# Revit family: HS497-68_disk-nerez_volné vřeteno DN100-RFA_2019
name_source: partatom
category: Pipe Accessories
units: mm (PartAtom-declared; Revit-internal decimal feet)

## family parameters
Always vertical = Yes
Cut with Voids When Loaded = No
Part Type = Valve - Breaks Into
Round Connector Dimension = Use Diameter
Shared = No
Work Plane-Based = No

## types (43) — shared parameters
CAT0 = Yes
G1 = 90 mm
G2 = 23 mm
G22 = 11 mm
L2D = 216 mm
L2D_Min = 3048 mm
QmdConnectorList = 301;D;302;D
SW21 = No
URL = http://www.hydronic.cz
W2D = 1000 mm
magiPartTypeId = 305
magiProductFamilyId = 53cea81e6f374d17b8841d9c72ad77

## per-type parameters (varying)
- HS 497-68_DN100_PN16_volné vřeteno: A1=99 mm; A2=17 mm; B2=56 mm; B2__ve=-56 mm  [stored -0.183727 ft]; D=100 mm; DD=13 mm; DD1=16 mm; DR=147 mm; DR2=50 mm; Description=Mezipřírubová uzavírací klapka s volným vřetenem; nerezový disk, DN100; PN16; kvs512; E21=10 mm; E22=20 mm; E23=5 mm  [stored 0.0164042 ft]; E4=125 mm; E42=63 mm; E44=31 mm; F=11 mm; G=90 mm; H=30 mm; L=52 mm; L1=42 mm; L2=26 mm; L41=19 mm; L41__ve=-19 mm; L42=96 mm; L42__ve=-96 mm  [stored -0.314961 ft]; L4R=13 mm; L4R__ve=-13 mm; LH1=73 mm; LHH1=47 mm; LHH3=2 mm  [stored 0.00656168 ft]; LHL=220 mm; M4=44 mm; M41=66 mm; MC Product Code=124 100 (nerezový disk, s volným vřetenem; DN100; PN16, kvs512); MM20=25 mm; Manufacturer=Hydronic Systems Prague s.r.o.; NC=50 mm; R=50 mm; SW1=Yes; SW2=No; SW20=No; SW3=No; SW30=No; Type Comments=mezipřírubová; nerezový disk; PN16; -10~+110°C (krátkodobě +120°C); X1=25 mm; X11=61 mm; magiProductId=65d1b245f4f142c78569c0602d5754
- HS 497-68_DN100_PN16_převodové kolo: A1=99 mm; A2=17 mm; B2=56 mm; B2__ve=-56 mm  [stored -0.183727 ft]; D=100 mm; DD=13 mm; DD1=16 mm; DR=147 mm; DR2=50 mm; Description=Mezipřírubová uzavírací klapka s převodovým kolem; nerezový disk, DN100; PN16; kvs512; E21=10 mm; E22=20 mm; E23=5 mm  [stored 0.0164042 ft]; E4=125 mm; E42=63 mm; E44=31 mm; F=11 mm; G=90 mm; H=30 mm; L=52 mm; L1=42 mm; L2=26 mm; L41=19 mm; L41__ve=-19 mm; L42=96 mm; L42__ve=-96 mm  [stored -0.314961 ft]; L4R=13 mm; L4R__ve=-13 mm; LH1=73 mm; LHH1=47 mm; LHH3=2 mm  [stored 0.00656168 ft]; LHL=220 mm; M4=44 mm; M41=65 mm; MC Product Code=126 100 (nerezový disk, s převodovým kolem; DN100; PN16, kvs512); MM20=25 mm; Manufacturer=Hydronic Systems Prague s.r.o.; NC=50 mm; R=50 mm; SW1=No; SW2=No; SW20=No; SW3=Yes; SW30=Yes; Type Comments=mezipřírubová; nerezový disk; PN16; -10~+110°C (krátkodobě +120°C); X1=25 mm; X11=61 mm; magiProductId=11e91b807e674d428c8e796fcdcfe2
- HS 497-68_DN100_PN16_s pákou: A1=99 mm; A2=17 mm; B2=56 mm; B2__ve=-56 mm  [stored -0.183727 ft]; D=100 mm; DD=13 mm; DD1=16 mm; DR=147 mm; DR2=50 mm; Description=Mezipřírubová uzavírací klapka s pákou; nerezový disk, DN100; PN16; kvs512; E21=12 mm; E22=24 mm; E23=6 mm; E4=125 mm; E42=63 mm; E44=31 mm; F=11 mm; G=90 mm; H=30 mm; L=52 mm; L1=42 mm; L2=26 mm; L41=19 mm; L41__ve=-19 mm; L42=96 mm; L42__ve=-96 mm  [stored -0.314961 ft]; L4R=13 mm; L4R__ve=-13 mm; LH1=87 mm; LHH1=57 mm; LHH3=3 mm  [stored 0.00984252 ft]; LHL=260 mm; M4=44 mm; M41=66 mm; MC Product Code=121 100 (nerezový disk, s pákou; DN100; PN16, kvs512); MM20=25 mm; Manufacturer=Hydronic Systems Prague s.r.o.; NC=50 mm; R=50 mm; SW1=No; SW2=Yes; SW20=Yes; SW3=No; SW30=No; Type Comments=mezipřírubová; nerezový disk; PN16; -10~+110°C (krátkodobě +120°C); X1=25 mm; X11=61 mm; magiProductId=28172f0b3f4b47b28323ac71cf8749
- HS 497-68_DN125_PN16_volné vřeteno: A1=100 mm; A2=18 mm; B2=64 mm; B2__ve=-64 mm  [stored -0.209974 ft]; D=125 mm; DD=13 mm; DD1=16 mm; DR=180 mm; DR2=63 mm; Description=Mezipřírubová uzavírací klapka s volným vřetenem; nerezový disk, DN125; PN16; kvs872; E21=10 mm; E22=20 mm; E23=5 mm  [stored 0.0164042 ft]; E4=125 mm; E42=63 mm; E44=31 mm; F=14 mm; G=90 mm; H=33 mm; L=56 mm; L1=45 mm; L2=28 mm; L41=19 mm; L41__ve=-19 mm; L42=96 mm; L42__ve=-96 mm  [stored -0.314961 ft]; L4R=13 mm; L4R__ve=-13 mm; LH1=73 mm; LHH1=47 mm; LHH3=2 mm  [stored 0.00656168 ft]; LHL=220 mm; M4=44 mm; M41=66 mm; MC Product Code=124 125 (nerezový disk, s volným vřetenem; DN125; PN16, kvs872); MM20=25 mm; Manufacturer=Hydronic Systems Prague s.r.o.; NC=50 mm; R=63 mm; SW1=Yes; SW2=No; SW20=No; SW3=No; SW30=No; Type Comments=mezipřírubová; nerezový disk; PN16; -10~+110°C (krátkodobě +120°C); X1=25 mm; X11=61 mm; magiProductId=0d813d910fc14f628bb3c2efbd185c
- HS 497-68_DN125_PN16_převodové kolo: A1=100 mm; A2=18 mm; B2=64 mm; B2__ve=-64 mm  [stored -0.209974 ft]; D=125 mm; DD=16 mm; DD1=20 mm; DR=180 mm; DR2=63 mm; Description=Mezipřírubová uzavírací klapka s převodovým kolem; nerezový disk, DN125; PN16; kvs872; E21=10 mm; E22=20 mm; E23=5 mm  [stored 0.0164042 ft]; E4=160 mm; E42=80 mm; E44=40 mm; F=14 mm; G=90 mm; H=33 mm; L=56 mm; L1=45 mm; L2=28 mm; L41=20 mm; L41__ve=-20 mm  [stored -0.0656168 ft]; L42=101 mm; L42__ve=-101 mm; L4R=14 mm; L4R__ve=-14 mm; LH1=73 mm; LHH1=47 mm; LHH3=2 mm  [stored 0.00656168 ft]; LHL=220 mm; M4=44 mm; M41=65 mm; MC Product Code=126125 (nerezový disk, s převodovým kolem; DN125; PN16, kvs872); MM20=25 mm; Manufacturer=Hydronic Systems Prague s.r.o.; NC=50 mm; R=63 mm; SW1=No; SW2=No; SW20=No; SW3=Yes; SW30=Yes; Type Comments=mezipřírubová; nerezový disk; PN16; -10~+110°C (krátkodobě +120°C); X1=25 mm; X11=61 mm; magiProductId=c56b7c13f372467684996fb1e0e229
- HS 497-68_DN125_PN16_s pákou: A1=100 mm; A2=18 mm; B2=64 mm; B2__ve=-64 mm  [stored -0.209974 ft]; D=125 mm; DD=13 mm; DD1=16 mm; DR=180 mm; DR2=63 mm; Description=Mezipřírubová uzavírací klapka s pákou; nerezový disk, DN125; PN16; kvs872; E21=15 mm; E22=30 mm; E23=8 mm; E4=125 mm; E42=63 mm; E44=31 mm; F=14 mm; G=90 mm; H=33 mm; L=56 mm; L1=45 mm; L2=28 mm; L41=19 mm; L41__ve=-19 mm; L42=96 mm; L42__ve=-96 mm  [stored -0.314961 ft]; L4R=13 mm; L4R__ve=-13 mm; LH1=105 mm; LHH1=71 mm; LHH3=4 mm  [stored 0.0131234 ft]; LHL=315 mm; M4=44 mm; M41=66 mm; MC Product Code=121 125 (nerezový disk, s pákou; DN125; PN16, kvs872); MM20=25 mm; Manufacturer=Hydronic Systems Prague s.r.o.; NC=50 mm; R=63 mm; SW1=No; SW2=Yes; SW20=Yes; SW3=No; SW30=No; Type Comments=mezipřírubová; nerezový disk; PN16; -10~+110°C (krátkodobě +120°C); X1=25 mm; X11=61 mm; magiProductId=105993c79a91492399feef7931321a
- HS 497-68_DN150_PN16_volné vřeteno: A1=99 mm; A2=19 mm; B2=58 mm; B2__ve=-58 mm  [stored -0.190289 ft]; D=150 mm; DD=13 mm; DD1=16 mm; DR=206 mm; DR2=75 mm; Description=Mezipřírubová uzavírací klapka s volným vřetenem; nerezový disk, DN150; PN16; kvs1347; E21=10 mm; E22=20 mm; E23=5 mm  [stored 0.0164042 ft]; E4=125 mm; E42=63 mm; E44=31 mm; F=14 mm; G=90 mm; H=33 mm; L=56 mm; L1=45 mm; L2=28 mm; L41=19 mm; L41__ve=-19 mm; L42=96 mm; L42__ve=-96 mm  [stored -0.314961 ft]; L4R=13 mm; L4R__ve=-13 mm; LH1=73 mm; LHH1=47 mm; LHH3=2 mm  [stored 0.00656168 ft]; LHL=220 mm; M4=44 mm; M41=66 mm; MC Product Code=124 150 (nerezový disk, s volným vřetenem; DN150; PN16, kvs1347); MM20=25 mm; Manufacturer=Hydronic Systems Prague s.r.o.; NC=50 mm; R=75 mm; SW1=Yes; SW2=No; SW20=No; SW3=No; SW30=No; Type Comments=mezipřírubová; nerezový disk; PN16; -10~+110°C (krátkodobě +120°C); X1=25 mm; X11=61 mm; magiProductId=50c80cb8ab434f55ab7796e5ac1331
- HS 497-68_DN150_PN16_převodové kolo: A1=99 mm; A2=19 mm; B2=58 mm; B2__ve=-58 mm  [stored -0.190289 ft]; D=150 mm; DD=16 mm; DD1=20 mm; DR=206 mm; DR2=75 mm; Description=Mezipřírubová uzavírací klapka s převodovým kolem; nerezový disk, DN150; PN16; kvs1347; E21=10 mm; E22=20 mm; E23=5 mm  [stored 0.0164042 ft]; E4=160 mm; E42=80 mm; E44=40 mm; F=14 mm; G=90 mm; H=33 mm; L=56 mm; L1=45 mm; L2=28 mm; L41=20 mm; L41__ve=-20 mm  [stored -0.0656168 ft]; L42=101 mm; L42__ve=-101 mm; L4R=14 mm; L4R__ve=-14 mm; LH1=73 mm; LHH1=47 mm; LHH3=2 mm  [stored 0.00656168 ft]; LHL=220 mm; M4=44 mm; M41=65 mm; MC Product Code=126 150 (nerezový disk, s převodovým kolem; DN150; PN16, kvs1347); MM20=25 mm; Manufacturer=Hydronic Systems Prague s.r.o.; NC=50 mm; R=75 mm; SW1=No; SW2=No; SW20=No; SW3=Yes; SW30=Yes; Type Comments=mezipřírubová; nerezový disk; PN16; -10~+110°C (krátkodobě +120°C); X1=25 mm; X11=61 mm; magiProductId=d94a1a0cf83b476eb10011b327f709
- HS 497-68_DN150_PN16_s pákou: A1=99 mm; A2=19 mm; B2=58 mm; B2__ve=-58 mm  [stored -0.190289 ft]; D=150 mm; DD=13 mm; DD1=16 mm; DR=206 mm; DR2=75 mm; Description=Mezipřírubová uzavírací klapka s pákou; nerezový disk, DN150; PN16; kvs1347; E21=15 mm; E22=30 mm; E23=8 mm; E4=125 mm; E42=63 mm; E44=31 mm; F=14 mm; G=90 mm; H=33 mm; L=56 mm; L1=45 mm; L2=28 mm; L41=19 mm; L41__ve=-19 mm; L42=96 mm; L42__ve=-96 mm  [stored -0.314961 ft]; L4R=13 mm; L4R__ve=-13 mm; LH1=105 mm; LHH1=71 mm; LHH3=4 mm  [stored 0.0131234 ft]; LHL=315 mm; M4=44 mm; M41=66 mm; MC Product Code=121 150 (nerezový disk, s pákou; DN150; PN16, kvs1347); MM20=25 mm; Manufacturer=Hydronic Systems Prague s.r.o.; NC=50 mm; R=75 mm; SW1=No; SW2=Yes; SW20=Yes; SW3=No; SW30=No; Type Comments=mezipřírubová; nerezový disk; PN16; -10~+110°C (krátkodobě +120°C); X1=25 mm; X11=61 mm; magiProductId=4d2835523fe84828bc50ff0a5a0dfb
- HS 497-68_DN200_PN16_volné vřeteno: A1=103 mm; A2=23 mm; B2=70 mm; B2__ve=-70 mm  [stored -0.229659 ft]; D=200 mm; DD=13 mm; DD1=16 mm; DR=257 mm; DR2=100 mm; Description=Mezipřírubová uzavírací klapka s volným vřetenem; nerezový disk, DN200; PN16; kvs2675; E21=10 mm; E22=20 mm; E23=5 mm  [stored 0.0164042 ft]; E4=125 mm; E42=63 mm; E44=31 mm; F=17 mm; G=90 mm; H=33 mm; L=60 mm; L1=48 mm; L2=30 mm; L41=19 mm; L41__ve=-19 mm; L42=96 mm; L42__ve=-96 mm  [stored -0.314961 ft]; L4R=13 mm; L4R__ve=-13 mm; LH1=73 mm; LHH1=47 mm; LHH3=2 mm  [stored 0.00656168 ft]; LHL=220 mm; M4=44 mm; M41=66 mm; MC Product Code=124 200 (nerezový disk, s volným vřetenem; DN200; PN16, kvs2675); MM20=25 mm; Manufacturer=Hydronic Systems Prague s.r.o.; NC=50 mm; R=100 mm; SW1=Yes; SW2=No; SW20=No; SW3=No; SW30=No; Type Comments=mezipřírubová; nerezový disk; PN16; -10~+110°C (krátkodobě +120°C); X1=25 mm; X11=61 mm; magiProductId=5b29029eaeba47139ee1055a4b9201
- HS 497-68_DN200_PN16_převodové kolo: A1=103 mm; A2=23 mm; B2=70 mm; B2__ve=-70 mm  [stored -0.229659 ft]; D=200 mm; DD=20 mm; DD1=25 mm; DR=257 mm; DR2=100 mm; Description=Mezipřírubová uzavírací klapka s převodovým kolem; nerezový disk, DN200; PN16; kvs2675; E21=10 mm; E22=20 mm; E23=5 mm  [stored 0.0164042 ft]; E4=200 mm; E42=100 mm; E44=50 mm; F=17 mm; G=90 mm; H=33 mm; L=60 mm; L1=48 mm; L2=30 mm; L41=23 mm; L41__ve=-23 mm; L42=114 mm; L42__ve=-114 mm  [stored -0.374016 ft]; L4R=15 mm; L4R__ve=-15 mm; LH1=73 mm; LHH1=47 mm; LHH3=2 mm  [stored 0.00656168 ft]; LHL=220 mm; M4=53 mm; M41=79 mm; MC Product Code=126 200 (nerezový disk, s převodovým kolem; DN200; PN16, kvs2675); MM20=25 mm; Manufacturer=Hydronic Systems Prague s.r.o.; NC=57 mm; R=100 mm; SW1=No; SW2=No; SW20=No; SW3=Yes; SW30=Yes; Type Comments=mezipřírubová; nerezový disk; PN16; -10~+110°C (krátkodobě +120°C); X1=25 mm; X11=61 mm; magiProductId=b2793cc1fcc44cf2a35062cd67c04f
- HS 497-68_DN200_PN16_s pákou: A1=103 mm; A2=23 mm; B2=70 mm; B2__ve=-70 mm  [stored -0.229659 ft]; D=200 mm; DD=13 mm; DD1=16 mm; DR=257 mm; DR2=100 mm; Description=Mezipřírubová uzavírací klapka s pákou; nerezový disk, DN200; PN16; kvs2675; E21=15 mm; E22=30 mm; E23=8 mm; E4=125 mm; E42=63 mm; E44=31 mm; F=17 mm; G=90 mm; H=33 mm; L=60 mm; L1=48 mm; L2=30 mm; L41=19 mm; L41__ve=-19 mm; L42=96 mm; L42__ve=-96 mm  [stored -0.314961 ft]; L4R=13 mm; L4R__ve=-13 mm; LH1=105 mm; LHH1=71 mm; LHH3=4 mm  [stored 0.0131234 ft]; LHL=315 mm; M4=44 mm; M41=66 mm; MC Product Code=121 200 (nerezový disk, s pákou; DN200; PN16, kvs2675); MM20=25 mm; Manufacturer=Hydronic Systems Prague s.r.o.; NC=50 mm; R=100 mm; SW1=No; SW2=Yes; SW20=Yes; SW3=No; SW30=No; Type Comments=mezipřírubová; nerezový disk; PN16; -10~+110°C (krátkodobě +120°C); X1=25 mm; X11=61 mm; magiProductId=f88d96c7af224537a51e72d7d8fffe
- HS 497-68_DN250_PN16_volné vřeteno: A1=129 mm; A2=28 mm; B2=85 mm; B2__ve=-85 mm  [stored -0.278871 ft]; D=250 mm; DD=13 mm; DD1=16 mm; DR=324 mm; DR2=125 mm; Description=Mezipřírubová uzavírací klapka s volným vřetenem; nerezový disk, DN250; PN16; kvs4555; E21=10 mm; E22=20 mm; E23=5 mm  [stored 0.0164042 ft]; E4=125 mm; E42=63 mm; E44=31 mm; F=22 mm; G=130 mm; H=23 mm; L=68 mm; L1=54 mm; L2=34 mm; L41=19 mm; L41__ve=-19 mm; L42=96 mm; L42__ve=-96 mm  [stored -0.314961 ft]; L4R=13 mm; L4R__ve=-13 mm; LH1=73 mm; LHH1=47 mm; LHH3=2 mm  [stored 0.00656168 ft]; LHL=220 mm; M4=44 mm; M41=66 mm; MC Product Code=124 250 (nerezový disk, s volným vřetenem; DN250; PN16, kvs4555); MM20=37 mm; Manufacturer=Hydronic Systems Prague s.r.o.; NC=50 mm; R=125 mm; SW1=Yes; SW2=No; SW20=No; SW3=No; SW30=No; Type Comments=mezipřírubová; nerezový disk; PN16; -10~+110°C (krátkodobě +120°C); X1=37 mm; X11=89 mm; magiProductId=b662e8305ca2402b9c510e66e6aa55
- HS 497-68_DN250_PN16_převodové kolo: A1=129 mm; A2=28 mm; B2=85 mm; B2__ve=-85 mm  [stored -0.278871 ft]; D=250 mm; DD=25 mm; DD1=31 mm; DR=324 mm; DR2=125 mm; Description=Mezipřírubová uzavírací klapka s převodovým kolem; nerezový disk, DN250; PN16; kvs4555; E21=10 mm; E22=20 mm; E23=5 mm  [stored 0.0164042 ft]; E4=250 mm; E42=125 mm; E44=63 mm; F=22 mm; G=130 mm; H=23 mm; L=68 mm; L1=54 mm; L2=34 mm; L41=33 mm; L41__ve=-33 mm  [stored -0.108268 ft]; L42=167 mm; L42__ve=-167 mm; L4R=22 mm; L4R__ve=-22 mm  [stored -0.0721785 ft]; LH1=73 mm; LHH1=47 mm; LHH3=2 mm  [stored 0.00656168 ft]; LHL=220 mm; M4=61 mm; M41=92 mm; MC Product Code=126 250 (nerezový disk, s převodovým kolem; DN250; PN16, kvs4555); MM20=37 mm; Manufacturer=Hydronic Systems Prague s.r.o.; NC=70 mm; R=125 mm; SW1=No; SW2=No; SW20=No; SW3=Yes; SW30=Yes; Type Comments=mezipřírubová; nerezový disk; PN16; -10~+110°C (krátkodobě +120°C); X1=37 mm; X11=89 mm; magiProductId=5ee9016806664ddfaa2632711f295c
- HS 497-68_DN300_PN16_volné vřeteno: A1=127 mm; A2=31 mm; B2=90 mm; B2__ve=-90 mm  [stored -0.295276 ft]; D=300 mm; DD=13 mm; DD1=16 mm; DR=376 mm; DR2=150 mm; Description=Mezipřírubová uzavírací klapka s volným vřetenem; nerezový disk, DN300; PN16; kvs7037; E21=10 mm; E22=20 mm; E23=5 mm  [stored 0.0164042 ft]; E4=125 mm; E42=63 mm; E44=31 mm; F=22 mm; G=130 mm; H=23 mm; L=78 mm; L1=62 mm; L2=39 mm; L41=19 mm; L41__ve=-19 mm; L42=96 mm; L42__ve=-96 mm  [stored -0.314961 ft]; L4R=13 mm; L4R__ve=-13 mm; LH1=73 mm; LHH1=47 mm; LHH3=2 mm  [stored 0.00656168 ft]; LHL=220 mm; M4=44 mm; M41=66 mm; MC Product Code=124 300 (nerezový disk, s volným vřetenem; DN300; PN16, kvs7037); MM20=37 mm; Manufacturer=Hydronic Systems Prague s.r.o.; NC=50 mm; R=150 mm; SW1=Yes; SW2=No; SW20=No; SW3=No; SW30=No; Type Comments=mezipřírubová; nerezový disk; PN16; -10~+110°C (krátkodobě +120°C); X1=37 mm; X11=89 mm; magiProductId=e1886f51ff004380a649519258edf2
- HS 497-68_DN300_PN16_převodové kolo: A1=127 mm; A2=31 mm; B2=90 mm; B2__ve=-90 mm  [stored -0.295276 ft]; D=300 mm; DD=25 mm; DD1=31 mm; DR=376 mm; DR2=150 mm; Description=Mezipřírubová uzavírací klapka s převodovým kolem; nerezový disk, DN300; PN16; kvs7037; E21=10 mm; E22=20 mm; E23=5 mm  [stored 0.0164042 ft]; E4=250 mm; E42=125 mm; E44=63 mm; F=22 mm; G=130 mm; H=23 mm; L=78 mm; L1=62 mm; L2=39 mm; L41=33 mm; L41__ve=-33 mm  [stored -0.108268 ft]; L42=167 mm; L42__ve=-167 mm; L4R=22 mm; L4R__ve=-22 mm  [stored -0.0721785 ft]; LH1=73 mm; LHH1=47 mm; LHH3=2 mm  [stored 0.00656168 ft]; LHL=220 mm; M4=61 mm; M41=92 mm; MC Product Code=126 300 (nerezový disk, s převodovým kolem; DN300; PN16, kvs7037); MM20=37 mm; Manufacturer=Hydronic Systems Prague s.r.o.; NC=70 mm; R=150 mm; SW1=No; SW2=No; SW20=No; SW3=Yes; SW30=Yes; Type Comments=mezipřírubová; nerezový disk; PN16; -10~+110°C (krátkodobě +120°C); X1=37 mm; X11=89 mm; magiProductId=6860f094f77d42088fbebc3c97f755
- HS 497-68_DN032_PN16_volné vřeteno: A1=76 mm; A2=10 mm; B2=44 mm; B2__ve=-44 mm  [stored -0.144357 ft]; D=32 mm; DD=13 mm; DD1=16 mm; DR=68 mm; DR2=16 mm; Description=Mezipřírubová uzavírací klapka s volným vřetenem; nerezový disk, DN32; PN16; kvs78; E21=10 mm; E22=20 mm; E23=5 mm  [stored 0.0164042 ft]; E4=125 mm; E42=63 mm; E44=31 mm; F=11 mm; G=90 mm; H=30 mm; L=33 mm; L1=26 mm; L2=17 mm; L41=19 mm; L41__ve=-19 mm; L42=96 mm; L42__ve=-96 mm  [stored -0.314961 ft]; L4R=13 mm; L4R__ve=-13 mm; LH1=73 mm; LHH1=47 mm; LHH3=2 mm  [stored 0.00656168 ft]; LHL=220 mm; M4=44 mm; M41=66 mm; MC Product Code=124 032 (nerezový disk, s volným vřetenem; DN32; PN16, kvs78); MM20=25 mm; Manufacturer=Hydronic Systems Prague s.r.o.; NC=50 mm; R=16 mm; SW1=Yes; SW2=No; SW20=No; SW3=No; SW30=No; Type Comments=mezipřírubová; nerezový disk; PN16; -10~+110°C (krátkodobě +120°C); X1=25 mm; X11=61 mm; magiProductId=8c5f65de52aa4067a77564107e31b2
- HS 497-68_DN032_PN16_převodové kolo: A1=76 mm; A2=10 mm; B2=44 mm; B2__ve=-44 mm  [stored -0.144357 ft]; D=32 mm; DD=13 mm; DD1=16 mm; DR=68 mm; DR2=16 mm; Description=Mezipřírubová uzavírací klapka s převodovým kolem; nerezový disk, DN32; PN16; kvs78; E21=10 mm; E22=20 mm; E23=5 mm  [stored 0.0164042 ft]; E4=125 mm; E42=63 mm; E44=31 mm; F=11 mm; G=90 mm; H=30 mm; L=33 mm; L1=26 mm; L2=17 mm; L41=19 mm; L41__ve=-19 mm; L42=96 mm; L42__ve=-96 mm  [stored -0.314961 ft]; L4R=13 mm; L4R__ve=-13 mm; LH1=73 mm; LHH1=47 mm; LHH3=2 mm  [stored 0.00656168 ft]; LHL=220 mm; M4=44 mm; M41=65 mm; MC Product Code=126 032 (nerezový disk, s převodovým kolem; DN32; PN16, kvs78); MM20=25 mm; Manufacturer=Hydronic Systems Prague s.r.o.; NC=50 mm; R=16 mm; SW1=No; SW2=No; SW20=No; SW3=Yes; SW30=Yes; Type Comments=mezipřírubová; nerezový disk; PN16; -10~+110°C (krátkodobě +120°C); X1=25 mm; X11=61 mm; magiProductId=60aaeffa8b3a4e809ef000e4660060
- HS 497-68_DN032_PN16_s pákou: A1=76 mm; A2=10 mm; B2=44 mm; B2__ve=-44 mm  [stored -0.144357 ft]; D=32 mm; DD=13 mm; DD1=16 mm; DR=68 mm; DR2=16 mm; Description=Mezipřírubová uzavírací klapka s pákou; nerezový disk, DN32; PN16; kvs78; E21=10 mm; E22=20 mm; E23=5 mm  [stored 0.0164042 ft]; E4=125 mm; E42=63 mm; E44=31 mm; F=11 mm; G=90 mm; H=30 mm; L=33 mm; L1=26 mm; L2=17 mm; L41=19 mm; L41__ve=-19 mm; L42=96 mm; L42__ve=-96 mm  [stored -0.314961 ft]; L4R=13 mm; L4R__ve=-13 mm; LH1=73 mm; LHH1=47 mm; LHH3=2 mm  [stored 0.00656168 ft]; LHL=220 mm; M4=44 mm; M41=66 mm; MC Product Code=121 032 (nerezový disk, s pákou; DN32; PN16, kvs78); MM20=25 mm; Manufacturer=Hydronic Systems Prague s.r.o.; NC=50 mm; R=16 mm; SW1=No; SW2=Yes; SW20=Yes; SW3=No; SW30=No; Type Comments=mezipřírubová; nerezový disk; PN16; -10~+110°C (krátkodobě +120°C); X1=25 mm; X11=61 mm; magiProductId=9ad8088d610749a1b871aa2aad8007
- HS 497-68_DN350_PN10_volné vřeteno: A1=130 mm; A2=34 mm; B2=88 mm; B2__ve=-88 mm  [stored -0.288714 ft]; D=350 mm; DD=13 mm; DD1=16 mm; DR=430 mm; DR2=175 mm; Description=Mezipřírubová uzavírací klapka s volným vřetenem; nerezový disk, DN350; PN10; kvs10165; E21=10 mm; E22=20 mm; E23=5 mm  [stored 0.0164042 ft]; E4=125 mm; E42=63 mm; E44=31 mm; F=22 mm; G=160 mm; H=31 mm; L=78 mm; L1=62 mm; L2=39 mm; L41=19 mm; L41__ve=-19 mm; L42=96 mm; L42__ve=-96 mm  [stored -0.314961 ft]; L4R=13 mm; L4R__ve=-13 mm; LH1=73 mm; LHH1=47 mm; LHH3=2 mm  [stored 0.00656168 ft]; LHL=220 mm; M4=44 mm; M41=66 mm; MC Product Code=124 350 (nerezový disk, s volným vřetenem; DN350; PN10, kvs10165); MM20=45 mm; Manufacturer=Hydronic Systems Prague s.r.o.; NC=50 mm; R=175 mm; SW1=Yes; SW2=No; SW20=No; SW3=No; SW30=No; Type Comments=mezipřírubová; nerezový disk; PN10; -10~+110°C (krátkodobě +120°C); X1=45 mm; X11=109 mm; magiProductId=72a1e05f22944421b7e9596a877137
- HS 497-68_DN350_PN10_převodové kolo: A1=130 mm; A2=34 mm; B2=88 mm; B2__ve=-88 mm  [stored -0.288714 ft]; D=350 mm; DD=25 mm; DD1=31 mm; DR=430 mm; DR2=175 mm; Description=Mezipřírubová uzavírací klapka s převodovým kolem; nerezový disk, DN350; PN10; kvs10165; E21=10 mm; E22=20 mm; E23=5 mm  [stored 0.0164042 ft]; E4=250 mm; E42=125 mm; E44=63 mm; F=22 mm; G=160 mm; H=31 mm; L=78 mm; L1=62 mm; L2=39 mm; L41=33 mm; L41__ve=-33 mm  [stored -0.108268 ft]; L42=167 mm; L42__ve=-167 mm; L4R=22 mm; L4R__ve=-22 mm  [stored -0.0721785 ft]; LH1=73 mm; LHH1=47 mm; LHH3=2 mm  [stored 0.00656168 ft]; LHL=220 mm; M4=61 mm; M41=92 mm; MC Product Code=126 350 (nerezový disk, s převodovým kolem; DN350; PN10, kvs10165); MM20=45 mm; Manufacturer=Hydronic Systems Prague s.r.o.; NC=70 mm; R=175 mm; SW1=No; SW2=No; SW20=No; SW3=Yes; SW30=Yes; Type Comments=mezipřírubová; nerezový disk; PN10; -10~+110°C (krátkodobě +120°C); X1=45 mm; X11=109 mm; magiProductId=a5a01426cb28494ba3afca92f1dace
- HS 497-68_DN400_PN10_volné vřeteno: A1=142 mm; A2=38 mm; B2=108 mm; B2__ve=-108 mm  [stored -0.354331 ft]; D=400 mm; DD=13 mm; DD1=16 mm; DR=485 mm; DR2=200 mm; Description=Mezipřírubová uzavírací klapka s volným vřetenem; nerezový disk, DN400; PN10; kvs13799; E21=10 mm; E22=20 mm; E23=5 mm  [stored 0.0164042 ft]; E4=125 mm; E42=63 mm; E44=31 mm; F=27 mm; G=160 mm; H=31 mm; L=102 mm; L1=82 mm; L2=51 mm; L41=19 mm; L41__ve=-19 mm; L42=96 mm; L42__ve=-96 mm  [stored -0.314961 ft]; L4R=13 mm; L4R__ve=-13 mm; LH1=73 mm; LHH1=47 mm; LHH3=2 mm  [stored 0.00656168 ft]; LHL=220 mm; M4=44 mm; M41=66 mm; MC Product Code=124 400 (nerezový disk, s volným vřetenem; DN400; PN10, kvs13799); MM20=45 mm; Manufacturer=Hydronic Systems Prague s.r.o.; NC=50 mm; R=200 mm; SW1=Yes; SW2=No; SW20=No; SW3=No; SW30=No; Type Comments=mezipřírubová; nerezový disk; PN10; -10~+110°C (krátkodobě +120°C); X1=45 mm; X11=109 mm; magiProductId=c70ebeb927c04ab99b176e257ad0a7
- HS 497-68_DN400_PN10_převodové kolo: A1=142 mm; A2=38 mm; B2=108 mm; B2__ve=-108 mm  [stored -0.354331 ft]; D=400 mm; DD=30 mm; DD1=38 mm; DR=485 mm; DR2=200 mm; Description=Mezipřírubová uzavírací klapka s převodovým kolem; nerezový disk, DN400; PN10; kvs13799; E21=10 mm; E22=20 mm; E23=5 mm  [stored 0.0164042 ft]; E4=300 mm; E42=150 mm; E44=75 mm; F=27 mm; G=160 mm; H=31 mm; L=102 mm; L1=82 mm; L2=51 mm; L41=42 mm; L41__ve=-42 mm; L42=209 mm; L42__ve=-209 mm; L4R=28 mm; L4R__ve=-28 mm; LH1=73 mm; LHH1=47 mm; LHH3=2 mm  [stored 0.00656168 ft]; LHL=220 mm; M4=69 mm; M41=104 mm; MC Product Code=126 400 (nerezový disk, s převodovým kolem; DN400; PN10, kvs13799); MM20=45 mm; Manufacturer=Hydronic Systems Prague s.r.o.; NC=73 mm; R=200 mm; SW1=No; SW2=No; SW20=No; SW3=Yes; SW30=Yes; Type Comments=mezipřírubová; nerezový disk; PN10; -10~+110°C (krátkodobě +120°C); X1=45 mm; X11=109 mm; magiProductId=cc64a4384dcb41b780d81810f4f293
- HS 497-68_DN040_PN16_volné vřeteno: A1=79 mm; A2=11 mm; B2=36 mm; B2__ve=-36 mm  [stored -0.11811 ft]; D=40 mm; DD=13 mm; DD1=16 mm; DR=76 mm; DR2=20 mm; Description=Mezipřírubová uzavírací klapka s volným vřetenem; nerezový disk, DN40; PN16; kvs78; E21=10 mm; E22=20 mm; E23=5 mm  [stored 0.0164042 ft]; E4=125 mm; E42=63 mm; E44=31 mm; F=11 mm; G=90 mm; H=30 mm; L=33 mm; L1=26 mm; L2=17 mm; L41=19 mm; L41__ve=-19 mm; L42=96 mm; L42__ve=-96 mm  [stored -0.314961 ft]; L4R=13 mm; L4R__ve=-13 mm; LH1=73 mm; LHH1=47 mm; LHH3=2 mm  [stored 0.00656168 ft]; LHL=220 mm; M4=44 mm; M41=66 mm; MC Product Code=124 040 (nerezový disk, s volným vřetenem; DN40; PN16, kvs78); MM20=25 mm; Manufacturer=Hydronic Systems Prague s.r.o.; NC=50 mm; R=20 mm; SW1=Yes; SW2=No; SW20=No; SW3=No; SW30=No; Type Comments=mezipřírubová; nerezový disk; PN16; -10~+110°C (krátkodobě +120°C); X1=25 mm; X11=61 mm; magiProductId=35f92312390745e88df5b5c325d9ee
- HS 497-68_DN040_PN16_převodové kolo: A1=79 mm; A2=11 mm; B2=36 mm; B2__ve=-36 mm  [stored -0.11811 ft]; D=40 mm; DD=13 mm; DD1=16 mm; DR=76 mm; DR2=20 mm; Description=Mezipřírubová uzavírací klapka s převodovým kolem; nerezový disk, DN40; PN16; kvs78; E21=10 mm; E22=20 mm; E23=5 mm  [stored 0.0164042 ft]; E4=125 mm; E42=63 mm; E44=31 mm; F=11 mm; G=90 mm; H=30 mm; L=33 mm; L1=26 mm; L2=17 mm; L41=19 mm; L41__ve=-19 mm; L42=96 mm; L42__ve=-96 mm  [stored -0.314961 ft]; L4R=13 mm; L4R__ve=-13 mm; LH1=73 mm; LHH1=47 mm; LHH3=2 mm  [stored 0.00656168 ft]; LHL=220 mm; M4=44 mm; M41=65 mm; MC Product Code=126 040 (nerezový disk, s převodovým kolem; DN40; PN16, kvs78); MM20=25 mm; Manufacturer=Hydronic Systems Prague s.r.o.; NC=50 mm; R=20 mm; SW1=No; SW2=No; SW20=No; SW3=Yes; SW30=Yes; Type Comments=mezipřírubová; nerezový disk; PN16; -10~+110°C (krátkodobě +120°C); X1=25 mm; X11=61 mm; magiProductId=d88e968eae3445bc9b7b4e6ff35127
- HS 497-68_DN040_PN16_s pákou: A1=79 mm; A2=11 mm; B2=36 mm; B2__ve=-36 mm  [stored -0.11811 ft]; D=40 mm; DD=13 mm; DD1=16 mm; DR=76 mm; DR2=20 mm; Description=Mezipřírubová uzavírací klapka s pákou; nerezový disk, DN40; PN16; kvs78; E21=10 mm; E22=20 mm; E23=5 mm  [stored 0.0164042 ft]; E4=125 mm; E42=63 mm; E44=31 mm; F=11 mm; G=90 mm; H=30 mm; L=33 mm; L1=26 mm; L2=17 mm; L41=19 mm; L41__ve=-19 mm; L42=96 mm; L42__ve=-96 mm  [stored -0.314961 ft]; L4R=13 mm; L4R__ve=-13 mm; LH1=73 mm; LHH1=47 mm; LHH3=2 mm  [stored 0.00656168 ft]; LHL=220 mm; M4=44 mm; M41=66 mm; MC Product Code=121 040 (nerezový disk, s pákou; DN40; PN16, kvs78); MM20=25 mm; Manufacturer=Hydronic Systems Prague s.r.o.; NC=50 mm; R=20 mm; SW1=No; SW2=Yes; SW20=Yes; SW3=No; SW30=No; Type Comments=mezipřírubová; nerezový disk; PN16; -10~+110°C (krátkodobě +120°C); X1=25 mm; X11=61 mm; magiProductId=c1b522ca65b4407a98818f232eaacb
- HS 497-68_DN450_PN10_volné vřeteno: A1=117 mm; A2=38 mm; B2=115 mm; B2__ve=-115 mm  [stored -0.377297 ft]; D=450 mm; DD=13 mm; DD1=16 mm; DR=536 mm; DR2=225 mm; Description=Mezipřírubová uzavírací klapka s volným vřetenem; nerezový, DN450; PN10; kvs18514; E21=10 mm; E22=20 mm; E23=5 mm  [stored 0.0164042 ft]; E4=125 mm; E42=63 mm; E44=31 mm; F=36 mm; G=190 mm; H=38 mm; L=114 mm; L1=91 mm; L2=57 mm; L41=19 mm; L41__ve=-19 mm; L42=96 mm; L42__ve=-96 mm  [stored -0.314961 ft]; L4R=13 mm; L4R__ve=-13 mm; LH1=73 mm; LHH1=47 mm; LHH3=2 mm  [stored 0.00656168 ft]; LHL=220 mm; M4=44 mm; M41=66 mm; MC Product Code=124 450 (nerezový disk, s volným vřetenem; DN450; PN10, kvs18514); MM20=54 mm; Manufacturer=Hydronic Systems Prague s.r.o.; NC=50 mm; R=225 mm; SW1=Yes; SW2=No; SW20=No; SW3=No; SW30=No; Type Comments=mezipřírubová; nerezový disk; PN10; -10~+110°C (krátkodobě +120°C); X1=54 mm; X11=130 mm; magiProductId=a8358bc282f14872b3194e530e590a
- HS 497-68_DN450_PN10_převodové kolo: A1=117 mm; A2=38 mm; B2=115 mm; B2__ve=-115 mm  [stored -0.377297 ft]; D=450 mm; DD=40 mm; DD1=50 mm; DR=536 mm; DR2=225 mm; Description=Mezipřírubová uzavírací klapka s převodovým kolem; nerezový disk, DN450; PN10; kvs18514; E21=10 mm; E22=20 mm; E23=5 mm  [stored 0.0164042 ft]; E4=400 mm; E42=200 mm; E44=100 mm; F=36 mm; G=190 mm; H=38 mm; L=114 mm; L1=91 mm; L2=57 mm; L41=48 mm; L41__ve=-48 mm; L42=241 mm; L42__ve=-241 mm; L4R=32 mm; L4R__ve=-32 mm; LH1=73 mm; LHH1=47 mm; LHH3=2 mm  [stored 0.00656168 ft]; LHL=220 mm; M4=97 mm; M41=145 mm; MC Product Code=126 450 (nerezový disk, s převodovým kolem; DN450; PN10, kvs18514); MM20=54 mm; Manufacturer=Zetkama; NC=92 mm; R=225 mm; SW1=No; SW2=No; SW20=No; SW3=Yes; SW30=Yes; Type Comments=mezipřírubová; nerezový disk; PN10; -10~+110°C (krátkodobě +120°C); X1=54 mm; X11=130 mm; magiProductId=cdf2d80f54a9414f9cbe50647c0ebd
- HS 497-68_DN500_PN10_volné vřeteno: A1=139 mm; A2=43 mm; B2=130 mm; B2__ve=-130 mm  [stored -0.426509 ft]; D=500 mm; DD=13 mm; DD1=16 mm; DR=593 mm; DR2=250 mm; Description=Mezipřírubová uzavírací klapka s volným vřetenem; nerezový disk, DN500; PN10; kvs23805; E21=10 mm; E22=20 mm; E23=5 mm  [stored 0.0164042 ft]; E4=125 mm; E42=63 mm; E44=31 mm; F=36 mm; G=210 mm; H=38 mm; L=127 mm; L1=102 mm; L2=64 mm; L41=19 mm; L41__ve=-19 mm; L42=96 mm; L42__ve=-96 mm  [stored -0.314961 ft]; L4R=13 mm; L4R__ve=-13 mm; LH1=73 mm; LHH1=47 mm; LHH3=2 mm  [stored 0.00656168 ft]; LHL=220 mm; M4=44 mm; M41=66 mm; MC Product Code=124 500 (nerezový disk, s volným vřetenem; DN500; PN10, kvs23805); MM20=59 mm; Manufacturer=Hydronic Systems Prague s.r.o.; NC=50 mm; R=250 mm; SW1=Yes; SW2=No; SW20=No; SW3=No; SW30=No; Type Comments=mezipřírubová; nerezový disk; PN10; -10~+110°C (krátkodobě +120°C); X1=59 mm; X11=143 mm; magiProductId=8c396e27bb2743f98f3c762b6517cd
- HS 497-68_DN500_PN10_převodové kolo: A1=139 mm; A2=43 mm; B2=130 mm; B2__ve=-130 mm  [stored -0.426509 ft]; D=500 mm; DD=40 mm; DD1=50 mm; DR=593 mm; DR2=250 mm; Description=Mezipřírubová uzavírací klapka s převodovým kolem; nerezový disk, DN500; PN10; kvs23805; E21=10 mm; E22=20 mm; E23=5 mm  [stored 0.0164042 ft]; E4=400 mm; E42=200 mm; E44=100 mm; F=36 mm; G=210 mm; H=38 mm; L=127 mm; L1=102 mm; L2=64 mm; L41=48 mm; L41__ve=-48 mm; L42=241 mm; L42__ve=-241 mm; L4R=32 mm; L4R__ve=-32 mm; LH1=73 mm; LHH1=47 mm; LHH3=2 mm  [stored 0.00656168 ft]; LHL=220 mm; M4=97 mm; M41=145 mm; MC Product Code=126 500 (nerezový disk, s převodovým kolem; DN500; PN10, kvs23805); MM20=59 mm; Manufacturer=Zetkama; NC=92 mm; R=250 mm; SW1=No; SW2=No; SW20=No; SW3=Yes; SW30=Yes; Type Comments=mezipřírubová; nerezový disk; PN10; -10~+110°C (krátkodobě +120°C); X1=59 mm; X11=143 mm; magiProductId=7647804f32e94cef828a7034a91a46
- HS 497-68_DN050_volné vřeteno: A1=83 mm; A2=12 mm; B2=37 mm; B2__ve=-37 mm; D=50 mm; DD=13 mm; DD1=16 mm; DR=100 mm; DR2=25 mm; Description=Mezipřírubová uzavírací klapka s volným vřetenem; nerezový disk, DN50; PN16; kvs98; E21=10 mm; E22=20 mm; E23=5 mm  [stored 0.0164042 ft]; E4=125 mm; E42=63 mm; E44=31 mm; F=11 mm; G=90 mm; H=30 mm; L=43 mm; L1=34 mm; L2=22 mm; L41=19 mm; L41__ve=-19 mm; L42=96 mm; L42__ve=-96 mm  [stored -0.314961 ft]; L4R=13 mm; L4R__ve=-13 mm; LH1=73 mm; LHH1=47 mm; LHH3=2 mm  [stored 0.00656168 ft]; LHL=220 mm; M4=44 mm; M41=66 mm; MC Product Code=124 050 (nerezový disk, s volným vřetenem; DN50; PN16, kvs98); MM20=25 mm; Manufacturer=Hydronic Systems Prague s.r.o.; NC=50 mm; R=25 mm; SW1=Yes; SW2=No; SW20=No; SW3=No; SW30=No; Type Comments=mezipřírubová; nerezový disk; PN16; -10~+110°C (krátkodobě +120°C); X1=25 mm; X11=61 mm; magiProductId=d71f296ecd6d4adf8f6e5d9853b4e0
- HS 497-68_DN050_PN16_převodové kolo: A1=83 mm; A2=12 mm; B2=37 mm; B2__ve=-37 mm; D=50 mm; DD=13 mm; DD1=16 mm; DR=100 mm; DR2=25 mm; Description=Mezipřírubová uzavírací klapka s převodovým kolem; nerezový disk, DN50; PN16; kvs98; E21=10 mm; E22=20 mm; E23=5 mm  [stored 0.0164042 ft]; E4=125 mm; E42=63 mm; E44=31 mm; F=11 mm; G=90 mm; H=30 mm; L=43 mm; L1=34 mm; L2=22 mm; L41=19 mm; L41__ve=-19 mm; L42=96 mm; L42__ve=-96 mm  [stored -0.314961 ft]; L4R=13 mm; L4R__ve=-13 mm; LH1=73 mm; LHH1=47 mm; LHH3=2 mm  [stored 0.00656168 ft]; LHL=220 mm; M4=44 mm; M41=65 mm; MC Product Code=126 050 (nerezový disk, s převodovým kolem; DN50; PN16, kvs98); MM20=25 mm; Manufacturer=Hydronic Systems Prague s.r.o.; NC=50 mm; R=25 mm; SW1=No; SW2=No; SW20=No; SW3=Yes; SW30=Yes; Type Comments=mezipřírubová; nerezový disk; PN16; -10~+110°C (krátkodobě +120°C); X1=25 mm; X11=61 mm; magiProductId=2fb080deeaed49c58418b94c1da5a4
- HS 497-68_DN050_PN16_s pákou: A1=83 mm; A2=12 mm; B2=37 mm; B2__ve=-37 mm; D=50 mm; DD=13 mm; DD1=16 mm; DR=100 mm; DR2=25 mm; Description=Mezipřírubová uzavírací klapka s pákou; nerezový disk, DN50; PN16; kvs98; E21=10 mm; E22=20 mm; E23=5 mm  [stored 0.0164042 ft]; E4=125 mm; E42=63 mm; E44=31 mm; F=11 mm; G=90 mm; H=30 mm; L=43 mm; L1=34 mm; L2=22 mm; L41=19 mm; L41__ve=-19 mm; L42=96 mm; L42__ve=-96 mm  [stored -0.314961 ft]; L4R=13 mm; L4R__ve=-13 mm; LH1=73 mm; LHH1=47 mm; LHH3=2 mm  [stored 0.00656168 ft]; LHL=220 mm; M4=44 mm; M41=66 mm; MC Product Code=121 050 (nerezový disk, s pákou; DN50; PN16, kvs98); MM20=25 mm; Manufacturer=Hydronic Systems Prague s.r.o.; NC=50 mm; R=25 mm; SW1=No; SW2=Yes; SW20=Yes; SW3=No; SW30=No; Type Comments=mezipřírubová; nerezový disk; PN16; -10~+110°C (krátkodobě +120°C); X1=25 mm; X11=61 mm; magiProductId=dabc632061f94877a994b9b4e68112
- HS 497-68_DN600_PN10_volné vřeteno: A1=145 mm; A2=49 mm; B2=140 mm; B2__ve=-140 mm  [stored -0.459318 ft]; D=600 mm; DD=13 mm; DD1=16 mm; DR=690 mm; DR2=300 mm; Description=Mezipřírubová uzavírací klapka s volným vřetenem; nerezový disk, DN600; PN10; kvs36788; E21=10 mm; E22=20 mm; E23=5 mm  [stored 0.0164042 ft]; E4=125 mm; E42=63 mm; E44=31 mm; F=60 mm; G=210 mm; H=80 mm; L=154 mm; L1=123 mm; L2=77 mm; L41=19 mm; L41__ve=-19 mm; L42=96 mm; L42__ve=-96 mm  [stored -0.314961 ft]; L4R=13 mm; L4R__ve=-13 mm; LH1=73 mm; LHH1=47 mm; LHH3=2 mm  [stored 0.00656168 ft]; LHL=220 mm; M4=44 mm; M41=66 mm; MC Product Code=124 600 (nerezový disk, s volným vřetenem; DN600; PN10, kvs36778); MM20=59 mm; Manufacturer=Hydronic Systems Prague s.r.o.; NC=50 mm; R=300 mm; SW1=Yes; SW2=No; SW20=No; SW3=No; SW30=No; Type Comments=mezipřírubová; nerezový disk; PN10; -10~+110°C (krátkodobě +120°C); X1=59 mm; X11=143 mm; magiProductId=99d5892c14664fce81a7c5903f7711
- HS 497-68_DN600_PN10_převodové kolo: A1=145 mm; A2=49 mm; B2=140 mm; B2__ve=-140 mm  [stored -0.459318 ft]; D=600 mm; DD=50 mm; DD1=63 mm; DR=690 mm; DR2=300 mm; Description=Mezipřírubová uzavírací klapka s převodovým kolem; nerezový disk, DN600; PN10; kvs36788; E21=10 mm; E22=20 mm; E23=5 mm  [stored 0.0164042 ft]; E4=500 mm; E42=250 mm; E44=125 mm; F=60 mm; G=210 mm; H=80 mm; L=154 mm; L1=123 mm; L2=77 mm; L41=61 mm; L41__ve=-61 mm; L42=306 mm; L42__ve=-306 mm  [stored -1.00394 ft]; L4R=41 mm; L4R__ve=-41 mm; LH1=73 mm; LHH1=47 mm; LHH3=2 mm  [stored 0.00656168 ft]; LHL=220 mm; M4=138 mm; M41=206 mm; MC Product Code=126 600 (nerezový disk, s převodovým kolem; DN600; PN10, kvs36778); MM20=59 mm; Manufacturer=Hydronic Systems Prague s.r.o.; NC=140 mm; R=300 mm; SW1=No; SW2=No; SW20=No; SW3=Yes; SW30=Yes; Type Comments=mezipřírubová; lnerezový disk; PN10; -10~+110°C (krátkodobě +120°C); X1=59 mm; X11=143 mm; magiProductId=b1e26faab48a4c499f6bb11e7e3002
- HS 497-68_DN065_PN16_volné vřeteno: A1=89 mm; A2=14 mm; B2=37 mm; B2__ve=-37 mm; D=65 mm; DD=13 mm; DD1=16 mm; DR=108 mm; DR2=33 mm; Description=Mezipřírubová uzavírací klapka s volným vřetenem; nerezový disk, DN65; PN16; kv167; E21=10 mm; E22=20 mm; E23=5 mm  [stored 0.0164042 ft]; E4=125 mm; E42=63 mm; E44=31 mm; F=11 mm; G=90 mm; H=30 mm; L=46 mm; L1=37 mm; L2=23 mm; L41=19 mm; L41__ve=-19 mm; L42=96 mm; L42__ve=-96 mm  [stored -0.314961 ft]; L4R=13 mm; L4R__ve=-13 mm; LH1=73 mm; LHH1=47 mm; LHH3=2 mm  [stored 0.00656168 ft]; LHL=220 mm; M4=44 mm; M41=66 mm; MC Product Code=124 065 (nerezový disk, s volným vřetenem; DN65; PN16, kvs167); MM20=25 mm; Manufacturer=Hydronic Systems Prague s.r.o.; NC=50 mm; R=33 mm; SW1=Yes; SW2=No; SW20=No; SW3=No; SW30=No; Type Comments=mezipřírubová; lnerezový disk; PN16; -10~+110°C (krátkodobě +120°C); X1=25 mm; X11=61 mm; magiProductId=5e5e208646e34ec29f889baab5d08e
- HS 497-68_DN065_PN16_převodové kolo: A1=89 mm; A2=14 mm; B2=37 mm; B2__ve=-37 mm; D=65 mm; DD=13 mm; DD1=16 mm; DR=108 mm; DR2=33 mm; Description=Mezipřírubová uzavírací klapka s převodovým kolem; nerezový disk, DN65; PN16; kvs167; E21=10 mm; E22=20 mm; E23=5 mm  [stored 0.0164042 ft]; E4=125 mm; E42=63 mm; E44=31 mm; F=11 mm; G=90 mm; H=30 mm; L=46 mm; L1=37 mm; L2=23 mm; L41=19 mm; L41__ve=-19 mm; L42=96 mm; L42__ve=-96 mm  [stored -0.314961 ft]; L4R=13 mm; L4R__ve=-13 mm; LH1=73 mm; LHH1=47 mm; LHH3=2 mm  [stored 0.00656168 ft]; LHL=220 mm; M4=44 mm; M41=65 mm; MC Product Code=126 065 (nerezový disk, s převodovým kolem; DN65; PN16, kvs167); MM20=25 mm; Manufacturer=Hydronic Systems Prague s.r.o.; NC=50 mm; R=33 mm; SW1=No; SW2=No; SW20=No; SW3=Yes; SW30=Yes; Type Comments=mezipřírubová; nerezový disk; PN16; -10~+110°C (krátkodobě +120°C); X1=25 mm; X11=61 mm; magiProductId=654d74c8d15540b0bfe523d988ccb3
- HS 497-68_DN065_PN16_s pákou: A1=89 mm; A2=14 mm; B2=37 mm; B2__ve=-37 mm; D=65 mm; DD=13 mm; DD1=16 mm; DR=108 mm; DR2=33 mm; Description=Mezipřírubová uzavírací klapka s pákou; nerezový disk, DN65; PN16; kvs167; E21=10 mm; E22=20 mm; E23=5 mm  [stored 0.0164042 ft]; E4=125 mm; E42=63 mm; E44=31 mm; F=11 mm; G=90 mm; H=30 mm; L=46 mm; L1=37 mm; L2=23 mm; L41=19 mm; L41__ve=-19 mm; L42=96 mm; L42__ve=-96 mm  [stored -0.314961 ft]; L4R=13 mm; L4R__ve=-13 mm; LH1=73 mm; LHH1=47 mm; LHH3=2 mm  [stored 0.00656168 ft]; LHL=220 mm; M4=44 mm; M41=66 mm; MC Product Code=121 065 (nerezový disk, s pákou; DN65; PN16, kvs167); MM20=25 mm; Manufacturer=Hydronic Systems Prague s.r.o.; NC=50 mm; R=33 mm; SW1=No; SW2=Yes; SW20=Yes; SW3=No; SW30=No; Type Comments=mezipřírubová; nerezový disk; PN16; -10~+110°C (krátkodobě +120°C); X1=25 mm; X11=61 mm; magiProductId=ebeb4b59db0641caaf6d6635ab37b9
- HS 497-68_DN080_PN16_volné vřeteno: A1=87 mm; A2=14 mm; B2=54 mm; B2__ve=-54 mm  [stored -0.177165 ft]; D=80 mm; DD=13 mm; DD1=16 mm; DR=124 mm; DR2=40 mm; Description=Mezipřírubová uzavírací klapka s volným vřetenem; nerezový disk, DN80; PN16; kvs258; E21=10 mm; E22=20 mm; E23=5 mm  [stored 0.0164042 ft]; E4=125 mm; E42=63 mm; E44=31 mm; F=11 mm; G=90 mm; H=30 mm; L=46 mm; L1=37 mm; L2=23 mm; L41=19 mm; L41__ve=-19 mm; L42=96 mm; L42__ve=-96 mm  [stored -0.314961 ft]; L4R=13 mm; L4R__ve=-13 mm; LH1=73 mm; LHH1=47 mm; LHH3=2 mm  [stored 0.00656168 ft]; LHL=220 mm; M4=44 mm; M41=66 mm; MC Product Code=124 080 (nerezový disk, s volným vřetenem; DN80; PN16, kvs258); MM20=25 mm; Manufacturer=Hydronic Systems Prague s.r.o.; NC=50 mm; R=40 mm; SW1=Yes; SW2=No; SW20=No; SW3=No; SW30=No; Type Comments=mezipřírubová; nerezový disk; PN16; -10~+110°C (krátkodobě +120°C); X1=25 mm; X11=61 mm; magiProductId=9e85c75c18654e1185a9c48ed6b00e
- HS 497-68_DN080_PN16_převodové kolo: A1=87 mm; A2=14 mm; B2=54 mm; B2__ve=-54 mm  [stored -0.177165 ft]; D=80 mm; DD=13 mm; DD1=16 mm; DR=124 mm; DR2=40 mm; Description=Mezipřírubová uzavírací klapka s převodovým kolem; nerezový disk, DN80; PN16; kvs258; E21=10 mm; E22=20 mm; E23=5 mm  [stored 0.0164042 ft]; E4=125 mm; E42=63 mm; E44=31 mm; F=11 mm; G=90 mm; H=30 mm; L=46 mm; L1=37 mm; L2=23 mm; L41=19 mm; L41__ve=-19 mm; L42=96 mm; L42__ve=-96 mm  [stored -0.314961 ft]; L4R=13 mm; L4R__ve=-13 mm; LH1=73 mm; LHH1=47 mm; LHH3=2 mm  [stored 0.00656168 ft]; LHL=220 mm; M4=44 mm; M41=65 mm; MC Product Code=126 080 (nerezový disk, s převodovým kolem; DN80; PN16, kvs258); MM20=25 mm; Manufacturer=Hydronic Systems Prague s.r.o.; NC=50 mm; R=40 mm; SW1=No; SW2=No; SW20=No; SW3=Yes; SW30=Yes; Type Comments=mezipřírubová; nerezový disk; PN16; -10~+110°C (krátkodobě +120°C); X1=25 mm; X11=61 mm; magiProductId=5b3c8238c3d041e68c75b199e7ea46
- HS 497-68_DN080_PN16_s pákou: A1=87 mm; A2=14 mm; B2=54 mm; B2__ve=-54 mm  [stored -0.177165 ft]; D=80 mm; DD=13 mm; DD1=16 mm; DR=124 mm; DR2=40 mm; Description=Mezipřírubová uzavírací klapka s pákou; nerezový disk, DN80; PN16; kvs258; E21=12 mm; E22=24 mm; E23=6 mm; E4=125 mm; E42=63 mm; E44=31 mm; F=11 mm; G=90 mm; H=30 mm; L=46 mm; L1=37 mm; L2=23 mm; L41=19 mm; L41__ve=-19 mm; L42=96 mm; L42__ve=-96 mm  [stored -0.314961 ft]; L4R=13 mm; L4R__ve=-13 mm; LH1=87 mm; LHH1=57 mm; LHH3=3 mm  [stored 0.00984252 ft]; LHL=260 mm; M4=44 mm; M41=66 mm; MC Product Code=121 080 (nerezový disk, s pákou; DN80; PN16, kvs258); MM20=25 mm; Manufacturer=Hydronic Systems Prague s.r.o.; NC=50 mm; R=40 mm; SW1=No; SW2=Yes; SW20=Yes; SW3=No; SW30=No; Type Comments=mezipřírubová; nerezový disk; PN16; -10~+110°C (krátkodobě +120°C); X1=25 mm; X11=61 mm; magiProductId=e414795fab0f4eccb99bc3572c5477
- HS 497-68_DN250_PN16_s pákou: A1=129 mm; A2=28 mm; B2=85 mm; B2__ve=-85 mm  [stored -0.278871 ft]; D=250 mm; DD=25 mm; DD1=31 mm; DR=324 mm; DR2=125 mm; Description=Mezipřírubová uzavírací klapka s pákou; nerezový disk, DN250; PN16; kvs4555; E21=10 mm; E22=20 mm; E23=5 mm  [stored 0.0164042 ft]; E4=250 mm; E42=125 mm; E44=63 mm; F=22 mm; G=130 mm; H=23 mm; L=68 mm; L1=54 mm; L2=34 mm; L41=33 mm; L41__ve=-33 mm  [stored -0.108268 ft]; L42=167 mm; L42__ve=-167 mm; L4R=22 mm; L4R__ve=-22 mm  [stored -0.0721785 ft]; LH1=73 mm; LHH1=47 mm; LHH3=2 mm  [stored 0.00656168 ft]; LHL=220 mm; M4=61 mm; M41=92 mm; MC Product Code=121 250 (nerezový disk, s ákou; DN250; PN16, kvs4555); MM20=37 mm; Manufacturer=Hydronic Systems Prague s.r.o.; NC=70 mm; R=125 mm; SW1=No; SW2=Yes; SW20=Yes; SW3=No; SW30=No; Type Comments=mezipřírubová; nerezový disk; PN16; -10~+110°C (krátkodobě +120°C); X1=37 mm; X11=89 mm
- HS 497-68_DN300_PN16_s pákou: A1=127 mm; A2=31 mm; B2=90 mm; B2__ve=-90 mm  [stored -0.295276 ft]; D=300 mm; DD=25 mm; DD1=31 mm; DR=376 mm; DR2=150 mm; Description=Mezipřírubová uzavírací klapka s pákou; nerezový disk, DN300; PN16; kvs7037; E21=10 mm; E22=20 mm; E23=5 mm  [stored 0.0164042 ft]; E4=250 mm; E42=125 mm; E44=63 mm; F=22 mm; G=130 mm; H=23 mm; L=78 mm; L1=62 mm; L2=39 mm; L41=33 mm; L41__ve=-33 mm  [stored -0.108268 ft]; L42=167 mm; L42__ve=-167 mm; L4R=22 mm; L4R__ve=-22 mm  [stored -0.0721785 ft]; LH1=73 mm; LHH1=47 mm; LHH3=2 mm  [stored 0.00656168 ft]; LHL=220 mm; M4=61 mm; M41=92 mm; MC Product Code=121 300 (nerezový disk, s pákou; DN300; PN16, kvs7037); MM20=37 mm; Manufacturer=Hydronic Systems Prague s.r.o.; NC=70 mm; R=150 mm; SW1=No; SW2=Yes; SW20=Yes; SW3=No; SW30=No; Type Comments=mezipřírubová; nerezový disk; PN16; -10~+110°C (krátkodobě +120°C); X1=37 mm; X11=89 mm

note: [stored X ft] marks values corroborated as IEEE doubles in the binary element streams (Revit-internal decimal feet)

## geometry (parser evidence)
native form markers: Sweep x1
no freeform markers — native parametric forms only
